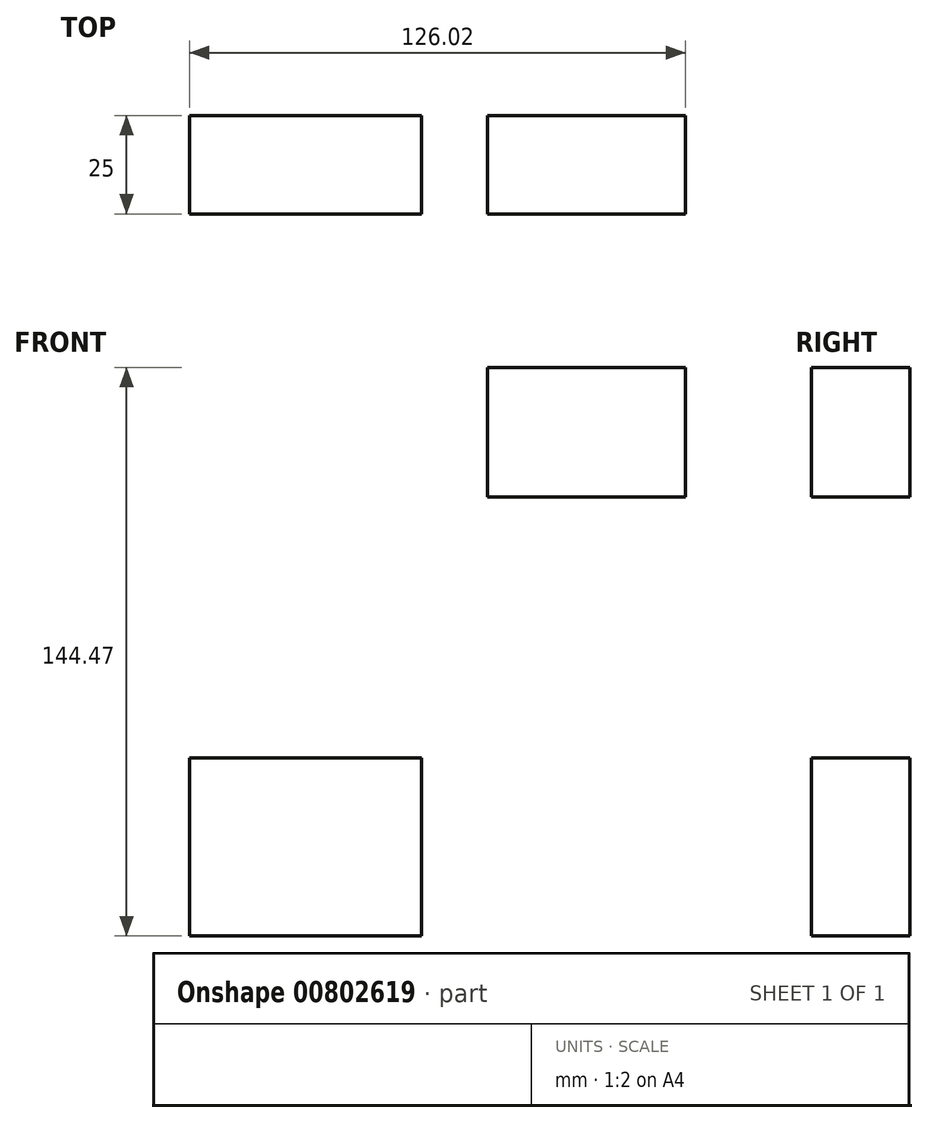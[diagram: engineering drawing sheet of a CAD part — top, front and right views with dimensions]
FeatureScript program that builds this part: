
annotation { "Feature Type Name" : "Feature", "Feature Type Description" : "" }
export const myFeature = defineFeature(function(context is Context, id is Id, definition is map)
    precondition{}
    {
        {
            var Q0;
            Q0=qCreatedBy(makeId("Front.planeOp"),FACE);
            var sketch = newSketch(context, id + "F0", { "sketchPlane" : qUnion([Q0])});
            skLineSegment(sketch, "E0.bottom", {"start": v(-34.56, 0) * mm, "end": v(24.44, 0) * mm});
            skLineSegment(sketch, "E0.top", {"start": v(-34.56, -45.3) * mm, "end": v(24.44, -45.3) * mm});
            skLineSegment(sketch, "E0.left", {"start": v(-34.56, 0) * mm, "end": v(-34.56, -45.3) * mm});
            skLineSegment(sketch, "E0.right", {"start": v(24.44, 0) * mm, "end": v(24.44, -45.3) * mm});
            skLineSegment(sketch, "E1.bottom", {"start": v(41.2, 99.16) * mm, "end": v(91.46, 99.16) * mm});
            skLineSegment(sketch, "E1.top", {"start": v(41.2, 66.2) * mm, "end": v(91.46, 66.2) * mm});
            skLineSegment(sketch, "E1.left", {"start": v(41.2, 99.16) * mm, "end": v(41.2, 66.2) * mm});
            skLineSegment(sketch, "E1.right", {"start": v(91.46, 99.16) * mm, "end": v(91.46, 66.2) * mm});
            skSolve(sketch);
        }
        {
            var Q0;
            Q0=makeQuery(id+"F0.imprint","IMPRINT",FACE,{"disambiguationData":[TD([[makeQuery(id+"F0.imprint","IMPRINT",EDGE,{"derivedFrom":sQuery(id+"F0.wireOp",EDGE,"E0.bottom")}),-1.0]])]});
            var Q1;
            Q1=makeQuery(id+"F0.imprint","IMPRINT",FACE,{"disambiguationData":[TD([[makeQuery(id+"F0.imprint","IMPRINT",EDGE,{"derivedFrom":sQuery(id+"F0.wireOp",EDGE,"E1.bottom")}),-1.0]])]});
            extrude(context, id + "F1", {"entities" : qUnion([Q0, Q1]), "depth" : 25 * mm, "offsetDistance" : 25 * mm});
        }
    });
